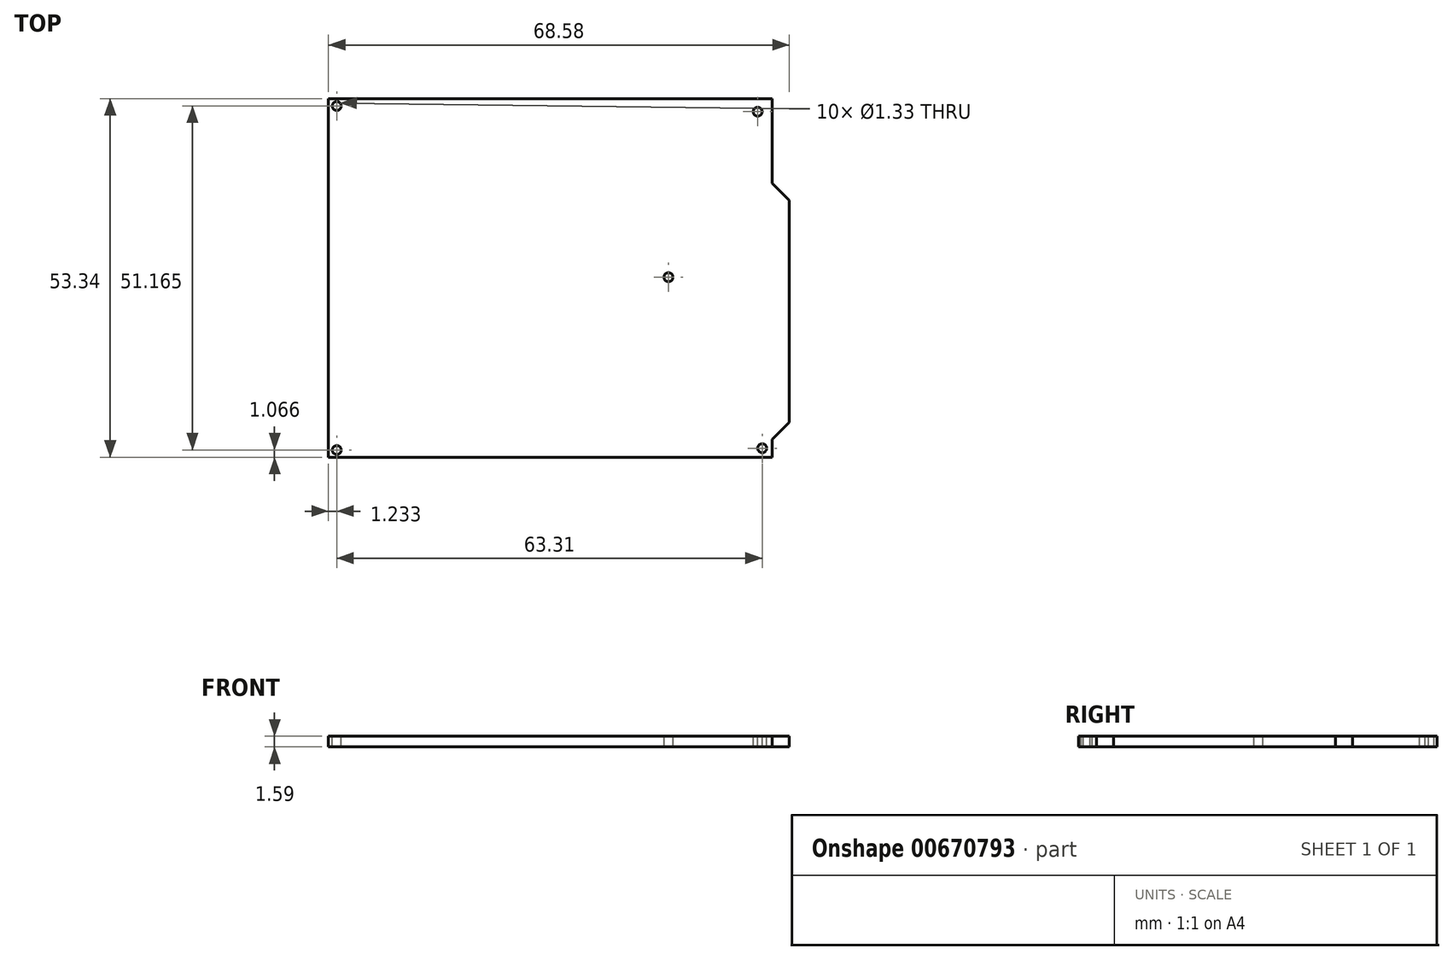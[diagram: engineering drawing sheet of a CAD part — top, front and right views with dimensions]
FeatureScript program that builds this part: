
annotation { "Feature Type Name" : "Feature", "Feature Type Description" : "" }
export const myFeature = defineFeature(function(context is Context, id is Id, definition is map)
    precondition{}
    {
        {
            var Q0;
            Q0=qCreatedBy(makeId("Top.planeOp"),FACE);
            var sketch = newSketch(context, id + "F0", { "sketchPlane" : qUnion([Q0])});
            skLineSegment(sketch, "E0", {"start": v(-33.02, 33.02) * mm, "end": v(33.02, 33.02) * mm});
            skLineSegment(sketch, "E1", {"start": v(33.02, 33.02) * mm, "end": v(33.02, -20.32) * mm});
            skLineSegment(sketch, "E2", {"start": v(33.02, -20.32) * mm, "end": v(-33.02, -20.32) * mm});
            skLineSegment(sketch, "E3", {"start": v(-33.02, -20.32) * mm, "end": v(-33.02, 33.02) * mm});
            skLineSegment(sketch, "E4", {"start": v(0, 0) * mm, "end": v(0, 33.02) * mm, "construction": true});
            skLineSegment(sketch, "E5", {"start": v(0, 0) * mm, "end": v(-33.02, 0) * mm, "construction": true});
            skLineSegment(sketch, "E6", {"start": v(33.02, 20.45) * mm, "end": v(35.56, 17.9) * mm});
            skLineSegment(sketch, "E7", {"start": v(35.56, 17.9) * mm, "end": v(35.56, -15.11) * mm});
            skLineSegment(sketch, "E8", {"start": v(35.56, -15.11) * mm, "end": v(33.02, -17.65) * mm});
            skSolve(sketch);
        }
        {
            var Q0;
            Q0 = qSketchRegion(id + "F0", true);
            extrude(context, id + "F1", {"entities" : qUnion([Q0]), "depth" : 1.59 * mm, "offsetDistance" : 25 * mm});
        }
        {
            var Q0;
            Q0=makeQuery(id+"F1.opExtrude","CAP_FACE",FACE,{"disambiguationData":[OSD([sQuery(id+"F0.wireOp",EDGE,"E0"),sQuery(id+"F0.wireOp",EDGE,"E1"),sQuery(id+"F0.wireOp",EDGE,"E2"),sQuery(id+"F0.wireOp",EDGE,"E3"),sQuery(id+"F0.wireOp",EDGE,"E6"),sQuery(id+"F0.wireOp",EDGE,"E7"),sQuery(id+"F0.wireOp",EDGE,"E8")])],"isStart":false});
            var sketch = newSketch(context, id + "F2", { "sketchPlane" : qUnion([Q0])});
            skCircle(sketch, "E9", {"center": v(-31.79, -19.25) * mm, "radius": 0.67 * mm});
            skCircle(sketch, "E10", {"center": v(31.52, -18.99) * mm, "radius": 0.67 * mm});
            skCircle(sketch, "E11", {"center": v(17.57, 6.46) * mm, "radius": 0.67 * mm});
            skCircle(sketch, "E12", {"center": v(30.84, 31.08) * mm, "radius": 0.67 * mm});
            skCircle(sketch, "E13", {"center": v(-31.79, 31.91) * mm, "radius": 0.67 * mm});
            skPoint(sketch, "E14", {"position": v(33.02, -18.99) * mm});
            skSolve(sketch);
        }
        {
            var Q0;
            Q0 = qSketchRegion(id + "F2", true);
            extrude(context, id + "F3", {"entities" : qUnion([Q0]), "operationType" : NewBodyOperationType.REMOVE, "oppositeDirection" : true, "depth" : 25 * mm, "offsetDistance" : 25 * mm});
        }
    });
